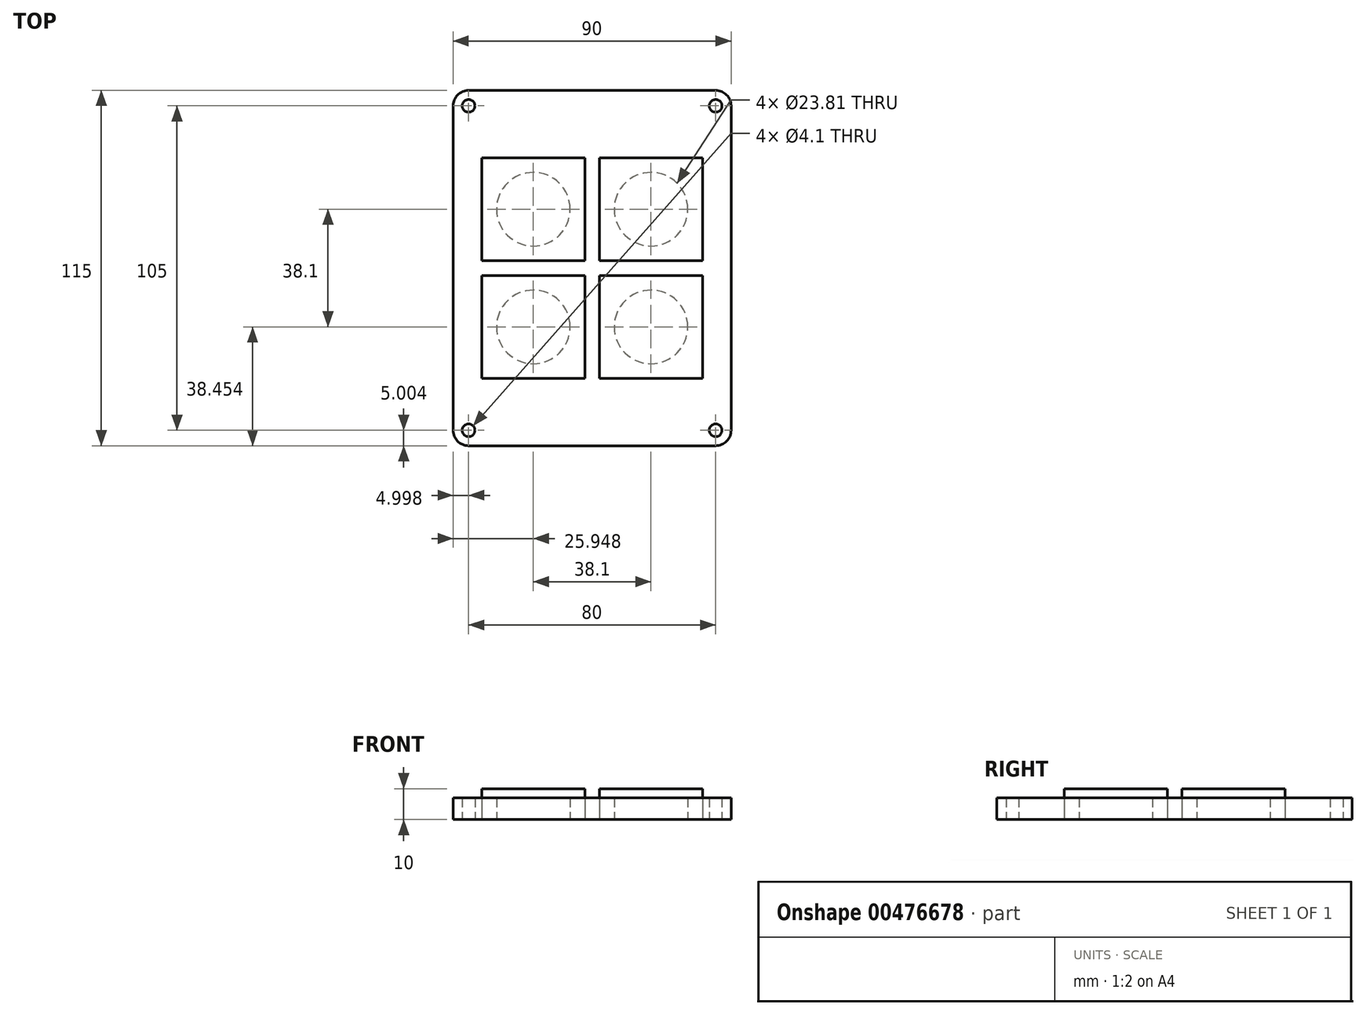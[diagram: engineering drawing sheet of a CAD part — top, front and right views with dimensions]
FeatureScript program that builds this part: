
annotation { "Feature Type Name" : "Feature", "Feature Type Description" : "" }
export const myFeature = defineFeature(function(context is Context, id is Id, definition is map)
    precondition{}
    {
        {
            var Q0;
            Q0=qCreatedBy(makeId("Top.planeOp"),FACE);
            var sketch = newSketch(context, id + "F0", { "sketchPlane" : qUnion([Q0])});
            skLineSegment(sketch, "E0.bottom", {"start": v(-95.96, 51.54) * mm, "end": v(-15.96, 51.54) * mm});
            skLineSegment(sketch, "E0.top", {"start": v(-95.96, -63.46) * mm, "end": v(-15.96, -63.46) * mm});
            skLineSegment(sketch, "E0.left", {"start": v(-100.96, 46.54) * mm, "end": v(-100.96, -58.46) * mm});
            skLineSegment(sketch, "E0.right", {"start": v(-10.96, 46.54) * mm, "end": v(-10.96, -58.46) * mm});
            skCircle(sketch, "E1", {"center": v(-95.96, 46.54) * mm, "radius": 2.05 * mm});
            skCircle(sketch, "E2.1.0.0", {"center": v(-15.96, 46.54) * mm, "radius": 2.05 * mm});
            skCircle(sketch, "E2.2.0.0", {"center": v(109.83, 44.3) * mm, "radius": 2.05 * mm});
            skCircle(sketch, "E3.0.1.0", {"center": v(-95.96, -58.46) * mm, "radius": 2.05 * mm});
            skCircle(sketch, "E4.2.0.0", {"center": v(109.83, -60.7) * mm, "radius": 2.05 * mm});
            skCircle(sketch, "E5.0.1.0", {"center": v(-15.96, -58.46) * mm, "radius": 2.05 * mm});
            skCircle(sketch, "E6", {"center": v(-75.01, -25) * mm, "radius": 11.9 * mm});
            skCircle(sketch, "E7.0.1.0", {"center": v(-75.01, 13.1) * mm, "radius": 11.9 * mm});
            skCircle(sketch, "E7.1.0.0", {"center": v(-36.91, -25) * mm, "radius": 11.9 * mm});
            skCircle(sketch, "E7.1.1.0", {"center": v(-36.91, 13.1) * mm, "radius": 11.9 * mm});
            skLineSegment(sketch, "E7.direction1", {"start": v(-75.01, -25) * mm, "end": v(-36.91, -25) * mm, "construction": true});
            skLineSegment(sketch, "E7.direction2", {"start": v(-75.01, -25) * mm, "end": v(-75.01, 13.1) * mm, "construction": true});
            skLineSegment(sketch, "E8.bottom", {"start": v(-91.68, -8.34) * mm, "end": v(-58.34, -8.34) * mm});
            skLineSegment(sketch, "E8.top", {"start": v(-91.68, -41.67) * mm, "end": v(-58.34, -41.67) * mm});
            skLineSegment(sketch, "E8.left", {"start": v(-91.68, -8.34) * mm, "end": v(-91.68, -41.67) * mm});
            skLineSegment(sketch, "E8.right", {"start": v(-58.34, -8.34) * mm, "end": v(-58.34, -41.67) * mm});
            skLineSegment(sketch, "E9.bottom", {"start": v(-53.58, -8.34) * mm, "end": v(-20.24, -8.34) * mm});
            skLineSegment(sketch, "E9.top", {"start": v(-53.58, -41.67) * mm, "end": v(-20.24, -41.67) * mm});
            skLineSegment(sketch, "E9.left", {"start": v(-53.58, -8.34) * mm, "end": v(-53.58, -41.67) * mm});
            skLineSegment(sketch, "E9.right", {"start": v(-20.24, -8.34) * mm, "end": v(-20.24, -41.67) * mm});
            skLineSegment(sketch, "E10.bottom", {"start": v(-53.58, 29.76) * mm, "end": v(-20.24, 29.76) * mm});
            skLineSegment(sketch, "E10.top", {"start": v(-53.58, -3.57) * mm, "end": v(-20.24, -3.57) * mm});
            skLineSegment(sketch, "E10.left", {"start": v(-53.58, 29.76) * mm, "end": v(-53.58, -3.57) * mm});
            skLineSegment(sketch, "E10.right", {"start": v(-20.24, 29.76) * mm, "end": v(-20.24, -3.57) * mm});
            skLineSegment(sketch, "E11.bottom", {"start": v(-91.68, 29.76) * mm, "end": v(-58.34, 29.76) * mm});
            skLineSegment(sketch, "E11.top", {"start": v(-91.68, -3.57) * mm, "end": v(-58.34, -3.57) * mm});
            skLineSegment(sketch, "E11.left", {"start": v(-91.68, 29.76) * mm, "end": v(-91.68, -3.57) * mm});
            skLineSegment(sketch, "E11.right", {"start": v(-58.34, 29.76) * mm, "end": v(-58.34, -3.57) * mm});
            skPoint(sketch, "E12.visualSharp", {"position": v(-100.96, 51.54) * mm});
            skArc(sketch, "E12.filletArc", {"start": v(-95.96, 51.54) * mm, "mid": v(-99.5, 50.08) * mm, "end": v(-100.96, 46.54) * mm});
            skPoint(sketch, "E13.visualSharp", {"position": v(-10.96, 51.54) * mm});
            skArc(sketch, "E13.filletArc", {"start": v(-10.96, 46.54) * mm, "mid": v(-12.43, 50.08) * mm, "end": v(-15.96, 51.54) * mm});
            skPoint(sketch, "E14.visualSharp", {"position": v(-10.96, -63.46) * mm});
            skArc(sketch, "E14.filletArc", {"start": v(-15.96, -63.46) * mm, "mid": v(-12.43, -62) * mm, "end": v(-10.96, -58.46) * mm});
            skPoint(sketch, "E15.visualSharp", {"position": v(-100.96, -63.46) * mm});
            skArc(sketch, "E15.filletArc", {"start": v(-100.96, -58.46) * mm, "mid": v(-99.5, -62) * mm, "end": v(-95.96, -63.46) * mm});
            skPoint(sketch, "E16", {"position": v(-55.96, -5.96) * mm});
            skSolve(sketch);
        }
        {
            var Q0;
            Q0=makeQuery(id+"F0.imprint","IMPRINT",FACE,{"disambiguationData":[TD([[makeQuery(id+"F0.imprint","IMPRINT",EDGE,{"derivedFrom":sQuery(id+"F0.wireOp",EDGE,"E0.bottom")}),-1.0]])]});
            var Q1;
            Q1=makeQuery(id+"F0.imprint","IMPRINT",FACE,{"disambiguationData":[TD([[makeQuery(id+"F0.imprint","IMPRINT",EDGE,{"derivedFrom":sQuery(id+"F0.wireOp",EDGE,"E7.0.1.0")}),-1.0]])]});
            var Q2;
            Q2=makeQuery(id+"F0.imprint","IMPRINT",FACE,{"disambiguationData":[TD([[makeQuery(id+"F0.imprint","IMPRINT",EDGE,{"derivedFrom":sQuery(id+"F0.wireOp",EDGE,"E7.1.1.0")}),-1.0]])]});
            var Q3;
            Q3=makeQuery(id+"F0.imprint","IMPRINT",FACE,{"disambiguationData":[TD([[makeQuery(id+"F0.imprint","IMPRINT",EDGE,{"derivedFrom":sQuery(id+"F0.wireOp",EDGE,"E6")}),-1.0]])]});
            var Q4;
            Q4=makeQuery(id+"F0.imprint","IMPRINT",FACE,{"disambiguationData":[TD([[makeQuery(id+"F0.imprint","IMPRINT",EDGE,{"derivedFrom":sQuery(id+"F0.wireOp",EDGE,"E7.1.0.0")}),-1.0]])]});
            extrude(context, id + "F1", {"entities" : qUnion([Q0, Q1, Q2, Q3, Q4]), "depth" : 7 * mm});
        }
        {
            var Q0;
            Q0=makeQuery(id+"F0.imprint","IMPRINT",FACE,{"disambiguationData":[TD([[makeQuery(id+"F0.imprint","IMPRINT",EDGE,{"derivedFrom":sQuery(id+"F0.wireOp",EDGE,"E7.1.1.0")}),-1.0]])]});
            var Q1;
            Q1=makeQuery(id+"F0.imprint","IMPRINT",FACE,{"disambiguationData":[TD([[makeQuery(id+"F0.imprint","IMPRINT",EDGE,{"derivedFrom":sQuery(id+"F0.wireOp",EDGE,"E7.0.1.0")}),-1.0]])]});
            var Q2;
            Q2=makeQuery(id+"F0.imprint","IMPRINT",FACE,{"disambiguationData":[TD([[makeQuery(id+"F0.imprint","IMPRINT",EDGE,{"derivedFrom":sQuery(id+"F0.wireOp",EDGE,"E7.0.1.0")}),1.0]])]});
            var Q3;
            Q3=makeQuery(id+"F0.imprint","IMPRINT",FACE,{"disambiguationData":[TD([[makeQuery(id+"F0.imprint","IMPRINT",EDGE,{"derivedFrom":sQuery(id+"F0.wireOp",EDGE,"E7.1.1.0")}),1.0]])]});
            var Q4;
            Q4=makeQuery(id+"F0.imprint","IMPRINT",FACE,{"disambiguationData":[TD([[makeQuery(id+"F0.imprint","IMPRINT",EDGE,{"derivedFrom":sQuery(id+"F0.wireOp",EDGE,"E7.1.0.0")}),1.0]])]});
            var Q5;
            Q5=makeQuery(id+"F0.imprint","IMPRINT",FACE,{"disambiguationData":[TD([[makeQuery(id+"F0.imprint","IMPRINT",EDGE,{"derivedFrom":sQuery(id+"F0.wireOp",EDGE,"E7.1.0.0")}),-1.0]])]});
            var Q6;
            Q6=makeQuery(id+"F0.imprint","IMPRINT",FACE,{"disambiguationData":[TD([[makeQuery(id+"F0.imprint","IMPRINT",EDGE,{"derivedFrom":sQuery(id+"F0.wireOp",EDGE,"E6")}),-1.0]])]});
            var Q7;
            Q7=makeQuery(id+"F0.imprint","IMPRINT",FACE,{"disambiguationData":[TD([[makeQuery(id+"F0.imprint","IMPRINT",EDGE,{"derivedFrom":sQuery(id+"F0.wireOp",EDGE,"E6")}),1.0]])]});
            extrude(context, id + "F2", {"entities" : qUnion([Q0, Q1, Q2, Q3, Q4, Q5, Q6, Q7]), "depth" : 10 * mm});
        }
    });
